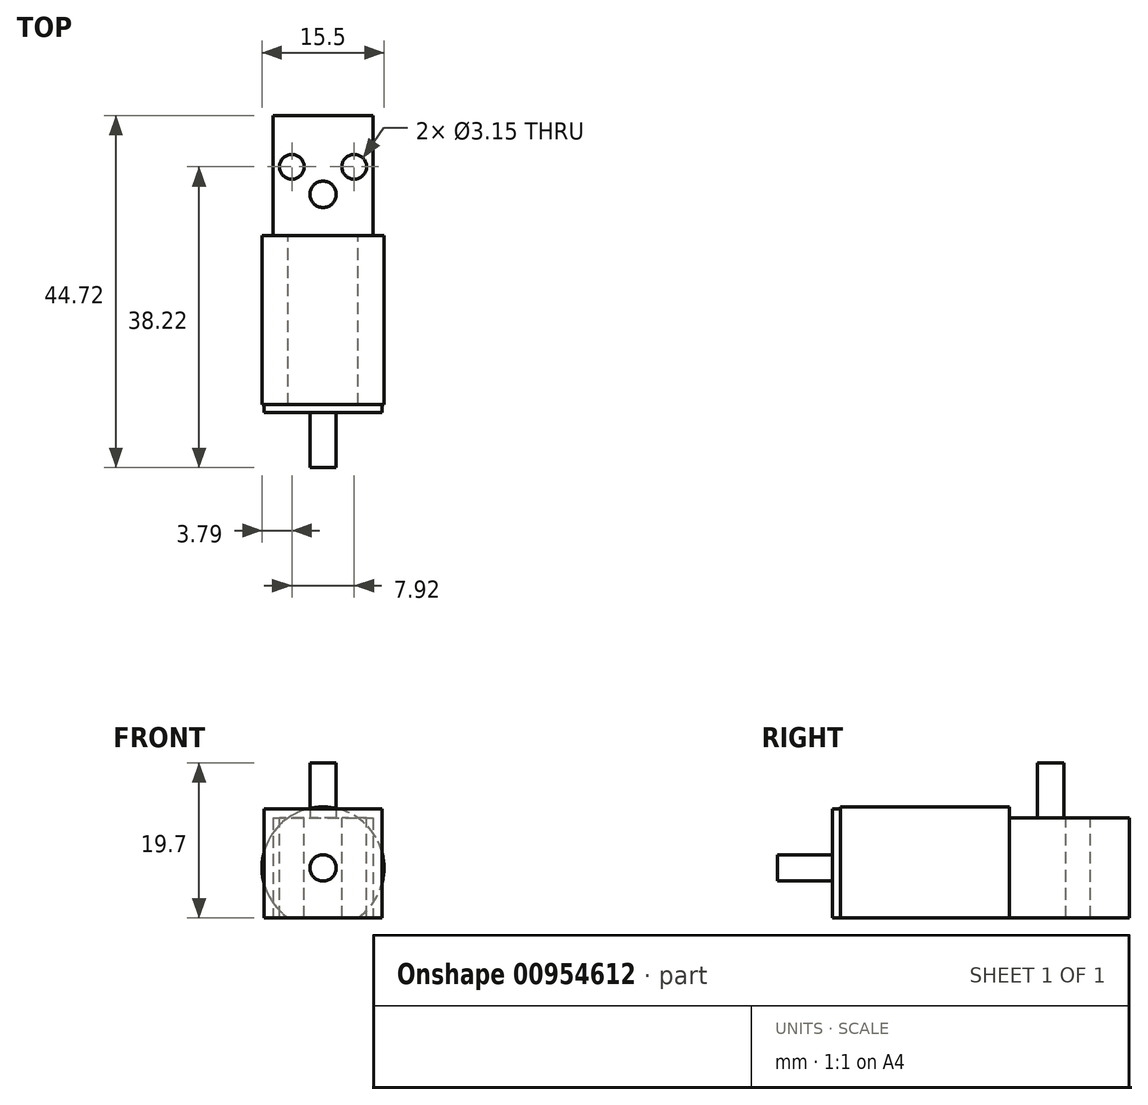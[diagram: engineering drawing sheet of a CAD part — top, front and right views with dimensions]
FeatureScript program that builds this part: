
annotation { "Feature Type Name" : "Feature", "Feature Type Description" : "" }
export const myFeature = defineFeature(function(context is Context, id is Id, definition is map)
    precondition{}
    {
        {
            var Q0;
            Q0=qCreatedBy(makeId("Front.planeOp"),FACE);
            var sketch = newSketch(context, id + "F0", { "sketchPlane" : qUnion([Q0])});
            skLineSegment(sketch, "E0.bottom", {"start": v(-6.35, 6.35) * mm, "end": v(6.35, 6.35) * mm});
            skLineSegment(sketch, "E0.top", {"start": v(-6.35, -6.35) * mm, "end": v(6.35, -6.35) * mm});
            skLineSegment(sketch, "E0.left", {"start": v(-6.35, 6.35) * mm, "end": v(-6.35, -6.35) * mm});
            skLineSegment(sketch, "E0.right", {"start": v(6.35, 6.35) * mm, "end": v(6.35, -6.35) * mm});
            skPoint(sketch, "E0.middle", {"position": v(0, 0) * mm});
            skSolve(sketch);
        }
        {
            var Q0;
            Q0=qSketchRegion(id+"F0",true);
            extrude(context, id + "F1", {"entities" : qUnion([Q0]), "oppositeDirection" : true, "depth" : 15.22 * mm, "offsetDistance" : 25 * mm});
        }
        {
            var Q0;
            Q0=makeQuery(id+"F1.opExtrude","SWEPT_FACE",FACE,{"disambiguationData":[OSD([sQuery(id+"F0.wireOp",EDGE,"E0.bottom")])]});
            var sketch = newSketch(context, id + "F2", { "sketchPlane" : qUnion([Q0])});
            skCircle(sketch, "E1", {"center": v(-3.96, 8.72) * mm, "radius": 1.57 * mm});
            skCircle(sketch, "E2", {"center": v(3.96, 8.72) * mm, "radius": 1.57 * mm});
            skSolve(sketch);
        }
        {
            var Q0;
            Q0=qSketchRegion(id+"F2",true);
            extrude(context, id + "F3", {"entities" : qUnion([Q0]), "operationType" : NewBodyOperationType.REMOVE, "endBound" : BoundingType.UP_TO_NEXT, "oppositeDirection" : true, "depth" : 25 * mm, "offsetDistance" : 25 * mm});
        }
        {
            var Q0;
            Q0=makeQuery(id+"F1.opExtrude","SWEPT_FACE",FACE,{"disambiguationData":[OSD([sQuery(id+"F0.wireOp",EDGE,"E0.bottom")])]});
            var sketch = newSketch(context, id + "F4", { "sketchPlane" : qUnion([Q0])});
            skCircle(sketch, "E3", {"center": v(0, 5.22) * mm, "radius": 1.67 * mm});
            skSolve(sketch);
        }
        {
            var Q0;
            Q0=makeQuery(id+"F4.imprint","IMPRINT",FACE,{"disambiguationData":[TD([[makeQuery(id+"F4.imprint","IMPRINT",EDGE,{"derivedFrom":sQuery(id+"F4.wireOp",EDGE,"E3")}),1.0]])]});
            extrude(context, id + "F5", {"entities" : qUnion([Q0]), "operationType" : NewBodyOperationType.ADD, "depth" : 7 * mm, "offsetDistance" : 25 * mm});
        }
        {
            var Q0;
            Q0=makeQuery(id+"F1.opExtrude","CAP_FACE",FACE,{"disambiguationData":[OSD([sQuery(id+"F0.wireOp",EDGE,"E0.bottom"),sQuery(id+"F0.wireOp",EDGE,"E0.top"),sQuery(id+"F0.wireOp",EDGE,"E0.left"),sQuery(id+"F0.wireOp",EDGE,"E0.right")])],"isStart":true});
            var sketch = newSketch(context, id + "F6", { "sketchPlane" : qUnion([Q0])});
            skCircle(sketch, "E4", {"center": v(0, 0) * mm, "radius": 7.75 * mm});
            skSolve(sketch);
        }
        {
            var Q0;
            Q0=qSketchRegion(id+"F6",true);
            extrude(context, id + "F7", {"entities" : qUnion([Q0]), "depth" : 21.5 * mm, "offsetDistance" : 25 * mm});
        }
        {
            var Q0;
            Q0=makeQuery(id+"F7.opExtrude","CAP_FACE",FACE,{"disambiguationData":[OSD([sQuery(id+"F6.wireOp",EDGE,"E4")])],"isStart":false});
            var sketch = newSketch(context, id + "F8", { "sketchPlane" : qUnion([Q0])});
            skLineSegment(sketch, "E5.bottom", {"start": v(7.5, 7.5) * mm, "end": v(-7.5, 7.5) * mm});
            skLineSegment(sketch, "E5.top", {"start": v(7.5, -7.5) * mm, "end": v(-7.5, -7.5) * mm});
            skLineSegment(sketch, "E5.left", {"start": v(7.5, 7.5) * mm, "end": v(7.5, -7.5) * mm});
            skLineSegment(sketch, "E5.right", {"start": v(-7.5, 7.5) * mm, "end": v(-7.5, -7.5) * mm});
            skPoint(sketch, "E5.middle", {"position": v(0, 0) * mm});
            skSolve(sketch);
        }
        {
            var Q0;
            {var subQ1=makeQuery(id+"F7.opExtrude","CAP_EDGE",EDGE,{"disambiguationData":[OSD([sQuery(id+"F6.wireOp",EDGE,"E4")])],"isStart":false});var subQ10=sQuery(id+"F8.wireOp",EDGE,"E5.bottom");var subQ11=makeQuery(id+"F8.imprint","INTERSECT",VERTEX,{"disambiguationData":[OD(0.0)],"derivedFrom":[subQ1,subQ10]});Q0=makeQuery(id+"F8.imprint","IMPRINT",FACE,{"disambiguationData":[TD([[makeQuery(id+"F8.imprint","IMPRINT",EDGE,{"disambiguationData":[TD([[subQ11,-1.0]])],"derivedFrom":subQ10}),1.0]])]});}
            var Q1;
            {var subQ0=sQuery(id+"F8.wireOp",EDGE,"E5.left");var subQ1=sQuery(id+"F8.wireOp",EDGE,"E5.bottom");var subQ2=makeQuery(id+"F8.imprint","INTERSECT",VERTEX,{"derivedFrom":[subQ1,subQ0]});Q1=makeQuery(id+"F8.imprint","IMPRINT",FACE,{"disambiguationData":[TD([[makeQuery(id+"F8.imprint","IMPRINT",EDGE,{"disambiguationData":[TD([[subQ2,-1.0]])],"derivedFrom":subQ1}),1.0]])]});}
            var Q2;
            {var subQ0=sQuery(id+"F8.wireOp",EDGE,"E5.right");var subQ1=sQuery(id+"F8.wireOp",EDGE,"E5.bottom");var subQ2=makeQuery(id+"F8.imprint","INTERSECT",VERTEX,{"derivedFrom":[subQ1,subQ0]});Q2=makeQuery(id+"F8.imprint","IMPRINT",FACE,{"disambiguationData":[TD([[makeQuery(id+"F8.imprint","IMPRINT",EDGE,{"disambiguationData":[TD([[subQ2,1.0]])],"derivedFrom":subQ1}),1.0]])]});}
            var Q3;
            {var subQ0=sQuery(id+"F8.wireOp",EDGE,"E5.left");var subQ1=sQuery(id+"F8.wireOp",EDGE,"E5.top");var subQ2=makeQuery(id+"F8.imprint","INTERSECT",VERTEX,{"derivedFrom":[subQ1,subQ0]});Q3=makeQuery(id+"F8.imprint","IMPRINT",FACE,{"disambiguationData":[TD([[makeQuery(id+"F8.imprint","IMPRINT",EDGE,{"disambiguationData":[TD([[subQ2,-1.0]])],"derivedFrom":subQ1}),-1.0]])]});}
            var Q4;
            {var subQ0=sQuery(id+"F8.wireOp",EDGE,"E5.right");var subQ1=sQuery(id+"F8.wireOp",EDGE,"E5.top");var subQ2=makeQuery(id+"F8.imprint","INTERSECT",VERTEX,{"derivedFrom":[subQ1,subQ0]});Q4=makeQuery(id+"F8.imprint","IMPRINT",FACE,{"disambiguationData":[TD([[makeQuery(id+"F8.imprint","IMPRINT",EDGE,{"disambiguationData":[TD([[subQ2,1.0]])],"derivedFrom":subQ1}),-1.0]])]});}
            extrude(context, id + "F9", {"entities" : qUnion([Q0, Q1, Q2, Q3, Q4]), "depth" : 1 * mm, "offsetDistance" : 25 * mm});
        }
        {
            var Q0;
            Q0=makeQuery(id+"F9.opExtrude","CAP_FACE",FACE,{"disambiguationData":[OSD([sQuery(id+"F8.wireOp",EDGE,"E5.bottom"),sQuery(id+"F8.wireOp",EDGE,"E5.top"),sQuery(id+"F8.wireOp",EDGE,"E5.left"),sQuery(id+"F8.wireOp",EDGE,"E5.right")])],"isStart":false});
            var sketch = newSketch(context, id + "F10", { "sketchPlane" : qUnion([Q0])});
            skCircle(sketch, "E6", {"center": v(0, 0) * mm, "radius": 1.68 * mm});
            skSolve(sketch);
        }
        {
            var Q0;
            Q0=qSketchRegion(id+"F10",true);
            extrude(context, id + "F11", {"entities" : qUnion([Q0]), "depth" : 7 * mm, "offsetDistance" : 25 * mm});
        }
        {
            var Q0;
            Q0=makeQuery(id+"F1.opExtrude","SWEPT_FACE",FACE,{"disambiguationData":[OSD([sQuery(id+"F0.wireOp",EDGE,"E0.top")])]});
            var sketch = newSketch(context, id + "F12", { "sketchPlane" : qUnion([Q0])});
            skLineSegment(sketch, "E7.bottom", {"start": v(-9.46, -19.26) * mm, "end": v(8.84, -19.26) * mm});
            skLineSegment(sketch, "E7.top", {"start": v(-9.46, 27.07) * mm, "end": v(8.84, 27.07) * mm});
            skLineSegment(sketch, "E7.left", {"start": v(-9.46, -19.26) * mm, "end": v(-9.46, 27.07) * mm});
            skLineSegment(sketch, "E7.right", {"start": v(8.84, -19.26) * mm, "end": v(8.84, 27.07) * mm});
            skSolve(sketch);
        }
        {
            var Q0;
            Q0=qSketchRegion(id+"F12",true);
            extrude(context, id + "F13", {"entities" : qUnion([Q0]), "operationType" : NewBodyOperationType.REMOVE, "depth" : 25 * mm, "offsetDistance" : 25 * mm});
        }
    });
